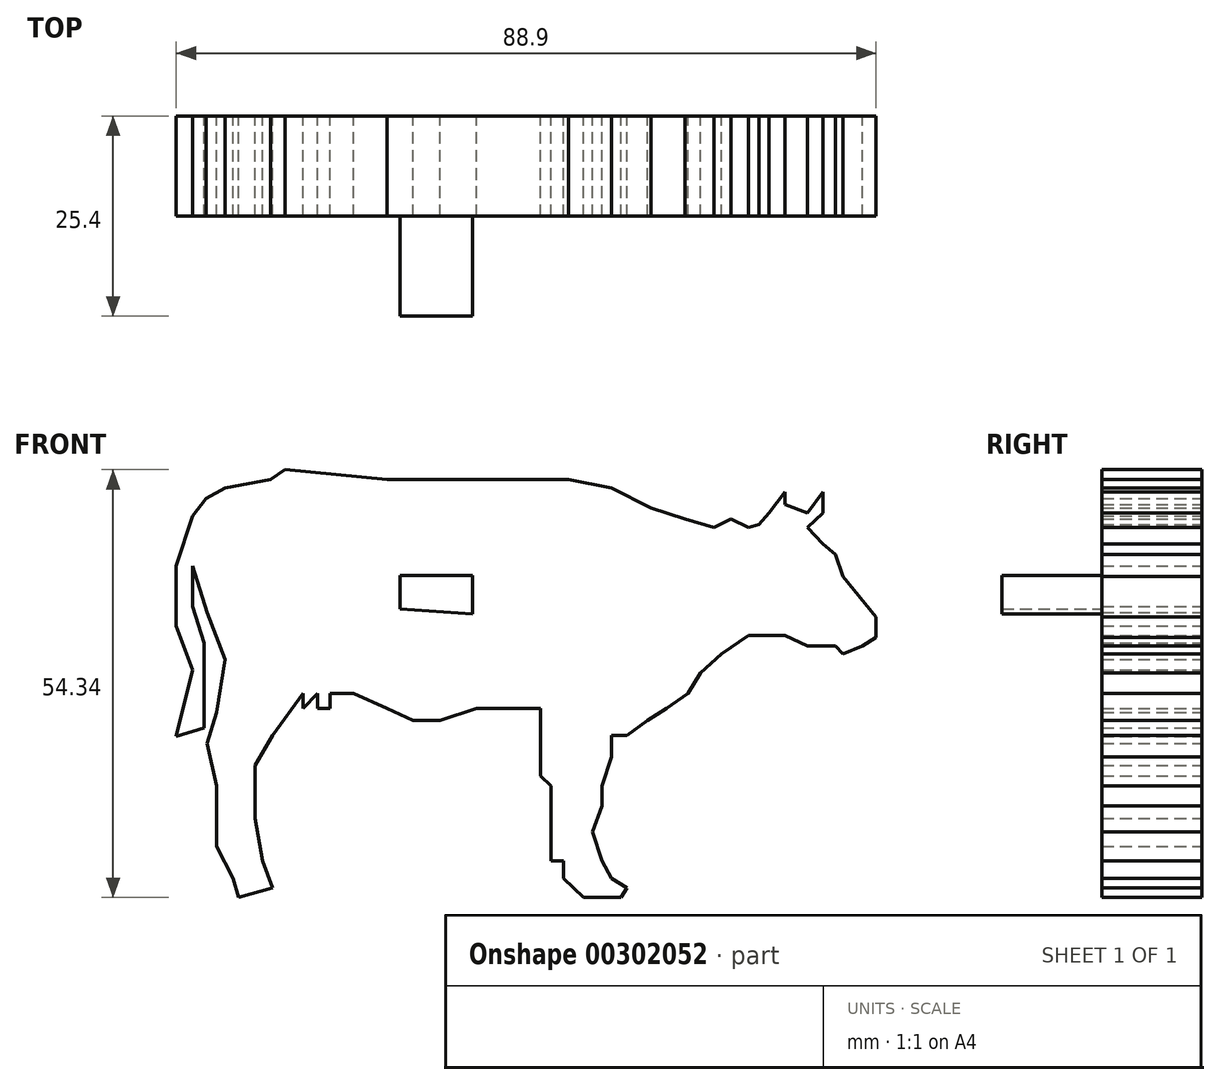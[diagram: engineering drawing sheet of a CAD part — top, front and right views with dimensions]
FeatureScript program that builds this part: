
annotation { "Feature Type Name" : "Feature", "Feature Type Description" : "" }
export const myFeature = defineFeature(function(context is Context, id is Id, definition is map)
    precondition{}
    {
        {
            var Q0;
            Q0=qCreatedBy(makeId("Front.planeOp"),FACE);
            var sketch = newSketch(context, id + "F0", { "sketchPlane" : qUnion([Q0])});
            skLineSegment(sketch, "E0", {"start": v(2.07, -1.26) * mm, "end": v(2.07, -1.4) * mm});
            skLineSegment(sketch, "E1", {"start": v(1.99, -1.26) * mm, "end": v(2.07, -1.26) * mm});
            skPoint(sketch, "E2", {"position": v(2.07, -1.26) * mm});
            skPoint(sketch, "E3.orphan", {"position": v(2.07, 49.54) * mm});
            skPoint(sketch, "E4.orphan", {"position": v(-48.73, -1.26) * mm});
            skPoint(sketch, "E5.orphan", {"position": v(2.07, -52.06) * mm});
            skPoint(sketch, "E6.orphan", {"position": v(52.87, -1.26) * mm});
            skPoint(sketch, "E7.orphan", {"position": v(46.44, -1.4) * mm});
            skLineSegment(sketch, "E8", {"start": v(-30.46, 24.49) * mm, "end": v(-36.27, 23.43) * mm});
            skLineSegment(sketch, "E9", {"start": v(-36.27, 23.43) * mm, "end": v(-38.64, 22.11) * mm});
            skLineSegment(sketch, "E10", {"start": v(-38.64, 22.11) * mm, "end": v(-40.36, 19.87) * mm});
            skLineSegment(sketch, "E11", {"start": v(-30.46, 24.49) * mm, "end": v(-28.62, 25.77) * mm});
            skLineSegment(sketch, "E12", {"start": v(-28.62, 25.77) * mm, "end": v(-15.69, 24.49) * mm});
            skLineSegment(sketch, "E13", {"start": v(-15.69, 24.49) * mm, "end": v(-8.3, 24.49) * mm});
            skLineSegment(sketch, "E14", {"start": v(-8.3, 24.49) * mm, "end": v(0.14, 24.49) * mm});
            skLineSegment(sketch, "E15", {"start": v(0.14, 24.49) * mm, "end": v(7.4, 24.49) * mm});
            skLineSegment(sketch, "E16", {"start": v(7.4, 24.49) * mm, "end": v(12.8, 23.43) * mm});
            skLineSegment(sketch, "E17", {"start": v(12.8, 23.43) * mm, "end": v(17.82, 20.92) * mm});
            skLineSegment(sketch, "E18", {"start": v(17.82, 20.92) * mm, "end": v(22.18, 19.47) * mm});
            skLineSegment(sketch, "E19", {"start": v(22.18, 19.47) * mm, "end": v(25.87, 18.42) * mm});
            skLineSegment(sketch, "E20", {"start": v(25.87, 18.42) * mm, "end": v(27.98, 19.47) * mm});
            skLineSegment(sketch, "E21", {"start": v(27.98, 19.47) * mm, "end": v(30.22, 18.42) * mm});
            skLineSegment(sketch, "E22", {"start": v(32.86, 20.26) * mm, "end": v(31.54, 18.81) * mm});
            skLineSegment(sketch, "E23", {"start": v(31.54, 18.81) * mm, "end": v(30.22, 18.42) * mm});
            skLineSegment(sketch, "E24", {"start": v(32.86, 20.26) * mm, "end": v(34.84, 22.9) * mm});
            skLineSegment(sketch, "E25", {"start": v(34.84, 21.32) * mm, "end": v(37.74, 20.26) * mm});
            skLineSegment(sketch, "E26", {"start": v(37.74, 20.26) * mm, "end": v(39.72, 22.9) * mm});
            skLineSegment(sketch, "E27", {"start": v(39.72, 22.9) * mm, "end": v(39.72, 20.26) * mm});
            skLineSegment(sketch, "E28", {"start": v(39.72, 20.26) * mm, "end": v(37.74, 18.42) * mm});
            skLineSegment(sketch, "E29", {"start": v(37.74, 18.42) * mm, "end": v(39.72, 16.3) * mm});
            skLineSegment(sketch, "E30", {"start": v(39.72, 16.3) * mm, "end": v(41.3, 14.99) * mm});
            skLineSegment(sketch, "E31", {"start": v(41.3, 14.99) * mm, "end": v(42.23, 12.22) * mm});
            skLineSegment(sketch, "E32", {"start": v(42.23, 12.22) * mm, "end": v(46.44, 7.07) * mm});
            skLineSegment(sketch, "E33", {"start": v(46.44, 7.07) * mm, "end": v(46.44, 4.43) * mm});
            skLineSegment(sketch, "E34", {"start": v(46.44, 4.43) * mm, "end": v(44.74, 3.38) * mm});
            skLineSegment(sketch, "E35", {"start": v(44.74, 3.38) * mm, "end": v(42.23, 2.32) * mm});
            skLineSegment(sketch, "E36", {"start": v(42.23, 2.32) * mm, "end": v(41.3, 3.38) * mm});
            skLineSegment(sketch, "E37", {"start": v(41.3, 3.38) * mm, "end": v(37.74, 3.38) * mm});
            skLineSegment(sketch, "E38", {"start": v(37.74, 3.38) * mm, "end": v(34.84, 4.7) * mm});
            skLineSegment(sketch, "E39", {"start": v(34.84, 4.7) * mm, "end": v(32.86, 4.7) * mm});
            skLineSegment(sketch, "E40", {"start": v(32.86, 4.7) * mm, "end": v(30.22, 4.7) * mm});
            skLineSegment(sketch, "E41", {"start": v(30.22, 4.7) * mm, "end": v(26.8, 2.32) * mm});
            skLineSegment(sketch, "E42", {"start": v(26.8, 2.32) * mm, "end": v(24.16, -0.05) * mm});
            skLineSegment(sketch, "E43", {"start": v(24.16, -0.05) * mm, "end": v(22.57, -2.7) * mm});
            skLineSegment(sketch, "E44", {"start": v(22.57, -2.7) * mm, "end": v(19.8, -4.54) * mm});
            skLineSegment(sketch, "E45", {"start": v(19.8, -4.54) * mm, "end": v(17.43, -6.12) * mm});
            skLineSegment(sketch, "E46", {"start": v(17.43, -6.12) * mm, "end": v(14.79, -7.97) * mm});
            skLineSegment(sketch, "E47", {"start": v(14.79, -7.97) * mm, "end": v(12.8, -7.97) * mm});
            skLineSegment(sketch, "E48", {"start": v(12.8, -7.97) * mm, "end": v(12.8, -10.74) * mm});
            skLineSegment(sketch, "E49", {"start": v(12.8, -10.74) * mm, "end": v(11.62, -14.43) * mm});
            skLineSegment(sketch, "E50", {"start": v(11.62, -14.43) * mm, "end": v(11.62, -16.94) * mm});
            skLineSegment(sketch, "E51", {"start": v(11.62, -16.94) * mm, "end": v(10.44, -20.24) * mm});
            skLineSegment(sketch, "E52", {"start": v(10.44, -20.24) * mm, "end": v(11.62, -23.93) * mm});
            skLineSegment(sketch, "E53", {"start": v(11.62, -23.93) * mm, "end": v(12.8, -26.17) * mm});
            skLineSegment(sketch, "E54", {"start": v(12.8, -26.17) * mm, "end": v(14.79, -27.36) * mm});
            skLineSegment(sketch, "E55", {"start": v(14.79, -27.36) * mm, "end": v(14.06, -28.57) * mm});
            skLineSegment(sketch, "E56", {"start": v(14.06, -28.57) * mm, "end": v(9.25, -28.57) * mm});
            skLineSegment(sketch, "E57", {"start": v(9.25, -28.57) * mm, "end": v(6.74, -26.17) * mm});
            skLineSegment(sketch, "E58", {"start": v(6.74, -26.17) * mm, "end": v(6.74, -23.93) * mm});
            skLineSegment(sketch, "E59", {"start": v(6.74, -23.93) * mm, "end": v(5.16, -23.93) * mm});
            skLineSegment(sketch, "E60", {"start": v(5.16, -23.93) * mm, "end": v(5.16, -18.52) * mm});
            skLineSegment(sketch, "E61", {"start": v(5.16, -18.52) * mm, "end": v(5.16, -14.43) * mm});
            skLineSegment(sketch, "E62", {"start": v(5.16, -14.43) * mm, "end": v(3.84, -13.11) * mm});
            skLineSegment(sketch, "E63", {"start": v(3.84, -13.11) * mm, "end": v(3.84, -7.97) * mm});
            skLineSegment(sketch, "E64", {"start": v(3.84, -7.97) * mm, "end": v(3.84, -4.54) * mm});
            skLineSegment(sketch, "E65", {"start": v(3.84, -4.54) * mm, "end": v(0.01, -4.54) * mm});
            skLineSegment(sketch, "E66", {"start": v(0.01, -4.54) * mm, "end": v(-4.34, -4.54) * mm});
            skLineSegment(sketch, "E67", {"start": v(-4.34, -4.54) * mm, "end": v(-8.96, -6.12) * mm});
            skLineSegment(sketch, "E68", {"start": v(-8.96, -6.12) * mm, "end": v(-12.39, -6.12) * mm});
            skLineSegment(sketch, "E69", {"start": v(-12.39, -6.12) * mm, "end": v(-15.69, -4.54) * mm});
            skLineSegment(sketch, "E70", {"start": v(-15.69, -4.54) * mm, "end": v(-19.9, -2.7) * mm});
            skLineSegment(sketch, "E71", {"start": v(-19.9, -2.7) * mm, "end": v(-22.94, -2.7) * mm});
            skLineSegment(sketch, "E72", {"start": v(-22.94, -2.7) * mm, "end": v(-22.94, -4.54) * mm});
            skLineSegment(sketch, "E73", {"start": v(-22.94, -4.54) * mm, "end": v(-24.53, -4.54) * mm});
            skLineSegment(sketch, "E74", {"start": v(-24.53, -4.54) * mm, "end": v(-24.53, -2.7) * mm});
            skLineSegment(sketch, "E75", {"start": v(-24.53, -2.7) * mm, "end": v(-26.37, -4.54) * mm});
            skLineSegment(sketch, "E76", {"start": v(-26.37, -4.54) * mm, "end": v(-26.37, -2.7) * mm});
            skLineSegment(sketch, "E77", {"start": v(-26.37, -2.7) * mm, "end": v(-30.2, -7.97) * mm});
            skLineSegment(sketch, "E78", {"start": v(-30.2, -7.97) * mm, "end": v(-32.44, -11.8) * mm});
            skLineSegment(sketch, "E79", {"start": v(-32.44, -11.8) * mm, "end": v(-32.44, -18.52) * mm});
            skLineSegment(sketch, "E80", {"start": v(-32.44, -18.52) * mm, "end": v(-31.52, -23.93) * mm});
            skLineSegment(sketch, "E81", {"start": v(-31.52, -23.93) * mm, "end": v(-30.2, -27.36) * mm});
            skLineSegment(sketch, "E82", {"start": v(-30.2, -27.36) * mm, "end": v(-34.55, -28.57) * mm});
            skLineSegment(sketch, "E83", {"start": v(-34.55, -28.57) * mm, "end": v(-35.22, -26.17) * mm});
            skLineSegment(sketch, "E84", {"start": v(-35.22, -26.17) * mm, "end": v(-37.32, -22.09) * mm});
            skLineSegment(sketch, "E85", {"start": v(-37.32, -22.09) * mm, "end": v(-37.32, -14.43) * mm});
            skLineSegment(sketch, "E86", {"start": v(-37.32, -14.43) * mm, "end": v(-38.5, -9.02) * mm});
            skLineSegment(sketch, "E87", {"start": v(-38.5, -9.02) * mm, "end": v(-37.32, -5.07) * mm});
            skLineSegment(sketch, "E88", {"start": v(-37.32, -5.07) * mm, "end": v(-36.27, 1.66) * mm});
            skLineSegment(sketch, "E89", {"start": v(-36.27, 1.66) * mm, "end": v(-38.5, 7.6) * mm});
            skLineSegment(sketch, "E90", {"start": v(-38.5, 7.6) * mm, "end": v(-40.36, 13.54) * mm});
            skLineSegment(sketch, "E91", {"start": v(-40.36, 13.54) * mm, "end": v(-40.36, 8.4) * mm});
            skLineSegment(sketch, "E92", {"start": v(-40.36, 8.4) * mm, "end": v(-38.92, 3.77) * mm});
            skLineSegment(sketch, "E93", {"start": v(-38.92, 3.77) * mm, "end": v(-38.92, -0.84) * mm});
            skLineSegment(sketch, "E94", {"start": v(-38.92, -0.84) * mm, "end": v(-38.92, -7.05) * mm});
            skPoint(sketch, "E94.endSnap0", {"position": v(-37.92, -7.05) * mm});
            skLineSegment(sketch, "E95", {"start": v(-38.92, -7.05) * mm, "end": v(-42.46, -8.15) * mm});
            skLineSegment(sketch, "E96", {"start": v(-42.46, -8.15) * mm, "end": v(-40.36, 0.34) * mm});
            skLineSegment(sketch, "E97", {"start": v(-40.36, 0.34) * mm, "end": v(-42.46, 5.88) * mm});
            skLineSegment(sketch, "E98", {"start": v(-42.46, 5.88) * mm, "end": v(-42.46, 13.54) * mm});
            skLineSegment(sketch, "E99", {"start": v(-42.46, 13.54) * mm, "end": v(-40.36, 19.87) * mm});
            skLineSegment(sketch, "E100", {"start": v(34.84, 22.9) * mm, "end": v(34.84, 21.32) * mm});
            skSolve(sketch);
        }
        {
            var Q0;
            Q0=makeQuery(id+"F0.imprint","IMPRINT",FACE,{"disambiguationData":[TD([[makeQuery(id+"F0.imprint","IMPRINT",EDGE,{"derivedFrom":sQuery(id+"F0.wireOp",EDGE,"E8")}),1.0]])]});
            extrude(context, id + "F1", {"entities" : qUnion([Q0]), "depth" : 12.7 * mm});
        }
        {
            var Q0;
            Q0=makeQuery(id+"F1.opExtrude","CAP_FACE",FACE,{"disambiguationData":[OSD([sQuery(id+"F0.wireOp",EDGE,"E8"),sQuery(id+"F0.wireOp",EDGE,"E9"),sQuery(id+"F0.wireOp",EDGE,"E10"),sQuery(id+"F0.wireOp",EDGE,"E11"),sQuery(id+"F0.wireOp",EDGE,"E12"),sQuery(id+"F0.wireOp",EDGE,"E13"),sQuery(id+"F0.wireOp",EDGE,"E14"),sQuery(id+"F0.wireOp",EDGE,"E15"),sQuery(id+"F0.wireOp",EDGE,"E16"),sQuery(id+"F0.wireOp",EDGE,"E17"),sQuery(id+"F0.wireOp",EDGE,"E18"),sQuery(id+"F0.wireOp",EDGE,"E19"),sQuery(id+"F0.wireOp",EDGE,"E20"),sQuery(id+"F0.wireOp",EDGE,"E21"),sQuery(id+"F0.wireOp",EDGE,"E22"),sQuery(id+"F0.wireOp",EDGE,"E23"),sQuery(id+"F0.wireOp",EDGE,"E24"),sQuery(id+"F0.wireOp",EDGE,"E25"),sQuery(id+"F0.wireOp",EDGE,"E26"),sQuery(id+"F0.wireOp",EDGE,"E27"),sQuery(id+"F0.wireOp",EDGE,"E28"),sQuery(id+"F0.wireOp",EDGE,"E29"),sQuery(id+"F0.wireOp",EDGE,"E30"),sQuery(id+"F0.wireOp",EDGE,"E31"),sQuery(id+"F0.wireOp",EDGE,"E32"),sQuery(id+"F0.wireOp",EDGE,"E33"),sQuery(id+"F0.wireOp",EDGE,"E34"),sQuery(id+"F0.wireOp",EDGE,"E35"),sQuery(id+"F0.wireOp",EDGE,"E36"),sQuery(id+"F0.wireOp",EDGE,"E37"),sQuery(id+"F0.wireOp",EDGE,"E38"),sQuery(id+"F0.wireOp",EDGE,"E39"),sQuery(id+"F0.wireOp",EDGE,"E40"),sQuery(id+"F0.wireOp",EDGE,"E41"),sQuery(id+"F0.wireOp",EDGE,"E42"),sQuery(id+"F0.wireOp",EDGE,"E43"),sQuery(id+"F0.wireOp",EDGE,"E44"),sQuery(id+"F0.wireOp",EDGE,"E45"),sQuery(id+"F0.wireOp",EDGE,"E46"),sQuery(id+"F0.wireOp",EDGE,"E47"),sQuery(id+"F0.wireOp",EDGE,"E48"),sQuery(id+"F0.wireOp",EDGE,"E49"),sQuery(id+"F0.wireOp",EDGE,"E50"),sQuery(id+"F0.wireOp",EDGE,"E51"),sQuery(id+"F0.wireOp",EDGE,"E52"),sQuery(id+"F0.wireOp",EDGE,"E53"),sQuery(id+"F0.wireOp",EDGE,"E54"),sQuery(id+"F0.wireOp",EDGE,"E55"),sQuery(id+"F0.wireOp",EDGE,"E56"),sQuery(id+"F0.wireOp",EDGE,"E57"),sQuery(id+"F0.wireOp",EDGE,"E58"),sQuery(id+"F0.wireOp",EDGE,"E59"),sQuery(id+"F0.wireOp",EDGE,"E60"),sQuery(id+"F0.wireOp",EDGE,"E61"),sQuery(id+"F0.wireOp",EDGE,"E62"),sQuery(id+"F0.wireOp",EDGE,"E63"),sQuery(id+"F0.wireOp",EDGE,"E64"),sQuery(id+"F0.wireOp",EDGE,"E65"),sQuery(id+"F0.wireOp",EDGE,"E66"),sQuery(id+"F0.wireOp",EDGE,"E67"),sQuery(id+"F0.wireOp",EDGE,"E68"),sQuery(id+"F0.wireOp",EDGE,"E69"),sQuery(id+"F0.wireOp",EDGE,"E70"),sQuery(id+"F0.wireOp",EDGE,"E71"),sQuery(id+"F0.wireOp",EDGE,"E72"),sQuery(id+"F0.wireOp",EDGE,"E73"),sQuery(id+"F0.wireOp",EDGE,"E74"),sQuery(id+"F0.wireOp",EDGE,"E75"),sQuery(id+"F0.wireOp",EDGE,"E76"),sQuery(id+"F0.wireOp",EDGE,"E77"),sQuery(id+"F0.wireOp",EDGE,"E78"),sQuery(id+"F0.wireOp",EDGE,"E79"),sQuery(id+"F0.wireOp",EDGE,"E80"),sQuery(id+"F0.wireOp",EDGE,"E81"),sQuery(id+"F0.wireOp",EDGE,"E82"),sQuery(id+"F0.wireOp",EDGE,"E83"),sQuery(id+"F0.wireOp",EDGE,"E84"),sQuery(id+"F0.wireOp",EDGE,"E85"),sQuery(id+"F0.wireOp",EDGE,"E86"),sQuery(id+"F0.wireOp",EDGE,"E87"),sQuery(id+"F0.wireOp",EDGE,"E88"),sQuery(id+"F0.wireOp",EDGE,"E89"),sQuery(id+"F0.wireOp",EDGE,"E90"),sQuery(id+"F0.wireOp",EDGE,"E91"),sQuery(id+"F0.wireOp",EDGE,"E92"),sQuery(id+"F0.wireOp",EDGE,"E93"),sQuery(id+"F0.wireOp",EDGE,"E94"),sQuery(id+"F0.wireOp",EDGE,"E95"),sQuery(id+"F0.wireOp",EDGE,"E96"),sQuery(id+"F0.wireOp",EDGE,"E97"),sQuery(id+"F0.wireOp",EDGE,"E98"),sQuery(id+"F0.wireOp",EDGE,"E99"),sQuery(id+"F0.wireOp",EDGE,"E100")])],"isStart":false});
            var sketch = newSketch(context, id + "F2", { "sketchPlane" : qUnion([Q0])});
            skLineSegment(sketch, "E101", {"start": v(-14, 8.08) * mm, "end": v(-14, 12.33) * mm});
            skLineSegment(sketch, "E102", {"start": v(-14, 12.33) * mm, "end": v(-4.84, 12.33) * mm});
            skLineSegment(sketch, "E103", {"start": v(-4.84, 12.33) * mm, "end": v(-4.84, 7.4) * mm});
            skLineSegment(sketch, "E104", {"start": v(-4.84, 7.4) * mm, "end": v(-14, 8.08) * mm});
            skSolve(sketch);
        }
        {
            var Q0;
            Q0 = qSketchRegion(id + "F2", true);
            extrude(context, id + "F3", {"entities" : qUnion([Q0]), "operationType" : NewBodyOperationType.ADD, "depth" : 12.7 * mm});
        }
    });
